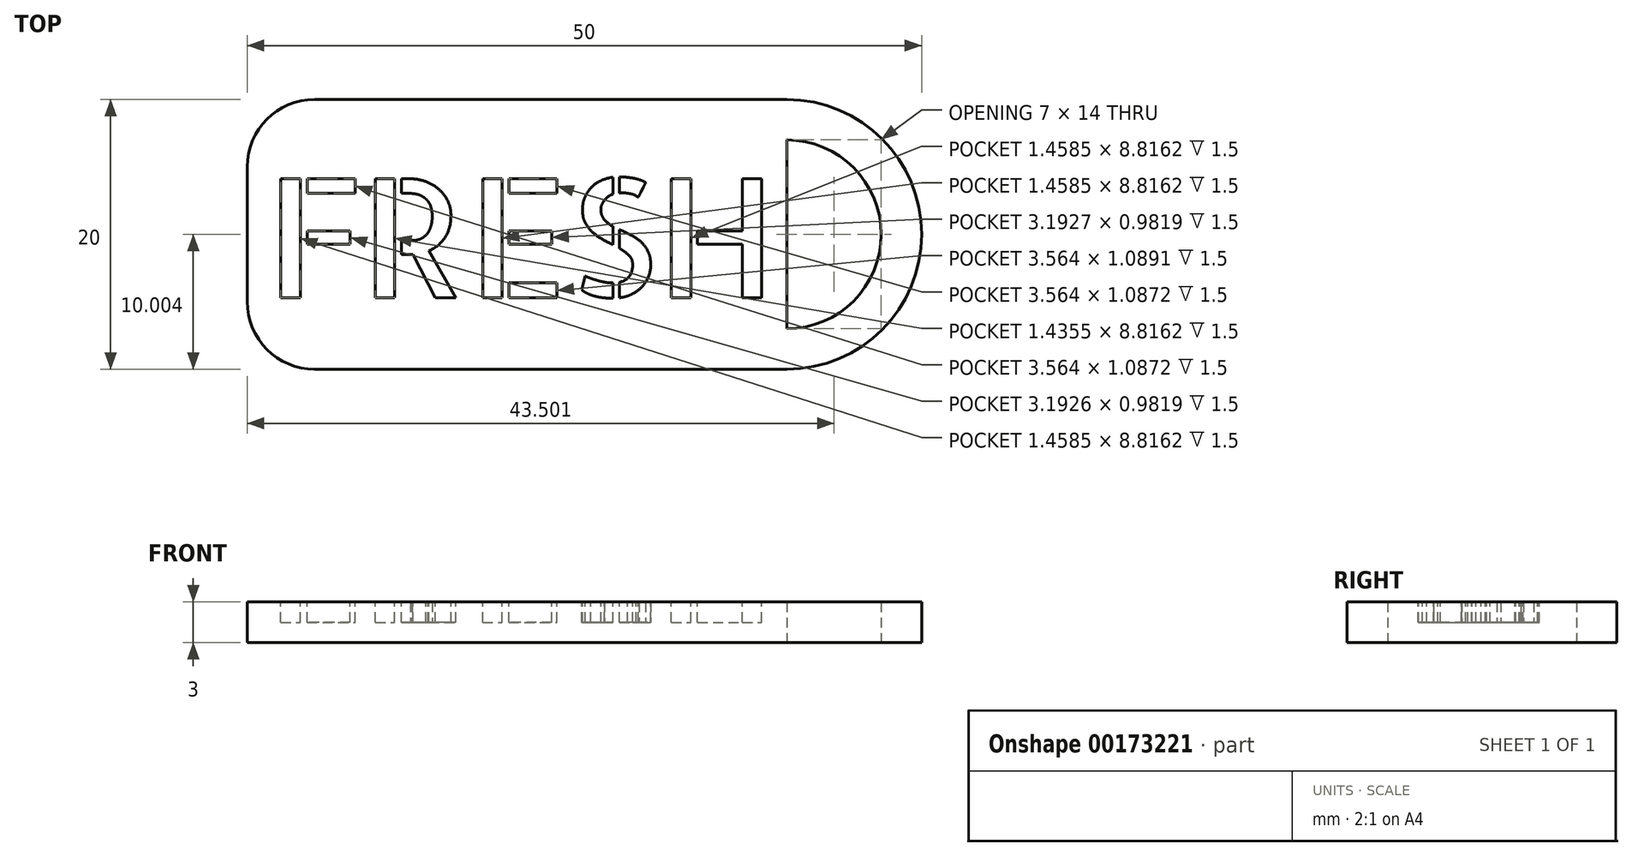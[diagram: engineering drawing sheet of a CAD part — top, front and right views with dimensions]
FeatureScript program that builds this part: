
annotation { "Feature Type Name" : "Feature", "Feature Type Description" : "" }
export const myFeature = defineFeature(function(context is Context, id is Id, definition is map)
    precondition{}
    {
        {
            var Q0;
            Q0=qCreatedBy(makeId("Top.planeOp"),FACE);
            var sketch = newSketch(context, id + "F0", { "sketchPlane" : qUnion([Q0])});
            skLineSegment(sketch, "E0.bottom", {"start": v(-15.52, 12.91) * mm, "end": v(19.48, 12.91) * mm});
            skLineSegment(sketch, "E0.top", {"start": v(-15.52, -7.09) * mm, "end": v(19.48, -7.09) * mm});
            skLineSegment(sketch, "E0.left", {"start": v(-20.52, 7.91) * mm, "end": v(-20.52, -2.09) * mm});
            skLineSegment(sketch, "E0.right", {"start": v(19.48, 12.91) * mm, "end": v(19.48, -7.09) * mm});
            skArc(sketch, "E1", {"start": v(19.48, -7.09) * mm, "mid": v(29.48, 2.91) * mm, "end": v(19.48, 12.91) * mm});
            skArc(sketch, "E2", {"start": v(19.48, -4.09) * mm, "mid": v(26.48, 2.91) * mm, "end": v(19.48, 9.91) * mm});
            skPoint(sketch, "E3.visualSharp", {"position": v(-20.52, 12.91) * mm});
            skArc(sketch, "E3.filletArc", {"start": v(-15.52, 12.91) * mm, "mid": v(-19.06, 11.45) * mm, "end": v(-20.52, 7.91) * mm});
            skPoint(sketch, "E4.visualSharp", {"position": v(-20.52, -7.09) * mm});
            skArc(sketch, "E4.filletArc", {"start": v(-20.52, -2.09) * mm, "mid": v(-19.06, -5.62) * mm, "end": v(-15.52, -7.09) * mm});
            skSolve(sketch);
        }
        {
            var Q0;
            {var subQ2=sQuery(id+"F0.wireOp",EDGE,"E0.bottom");Q0=makeQuery(id+"F0.imprint","IMPRINT",FACE,{"disambiguationData":[TD([[makeQuery(id+"F0.imprint","IMPRINT",EDGE,{"derivedFrom":subQ2}),-1.0]])]});}
            var Q1;
            {var subQ0=sQuery(id+"F0.wireOp",EDGE,"E1");Q1=makeQuery(id+"F0.imprint","IMPRINT",FACE,{"disambiguationData":[TD([[makeQuery(id+"F0.imprint","IMPRINT",EDGE,{"derivedFrom":subQ0}),1.0]])]});}
            extrude(context, id + "F1", {"entities" : qUnion([Q0, Q1]), "depth" : 3 * mm});
        }
        {
            var Q0;
            Q0=makeQuery(id+"F1.opExtrude","CAP_FACE",FACE,{"disambiguationData":[OSD([sQuery(id+"F0.wireOp",EDGE,"E0.bottom"),sQuery(id+"F0.wireOp",EDGE,"E0.top"),sQuery(id+"F0.wireOp",EDGE,"E0.left"),sQuery(id+"F0.wireOp",EDGE,"E0.right"),sQuery(id+"F0.wireOp",EDGE,"E1"),sQuery(id+"F0.wireOp",EDGE,"E2"),sQuery(id+"F0.wireOp",EDGE,"E3.filletArc"),sQuery(id+"F0.wireOp",EDGE,"E4.filletArc")])],"isStart":false});
            var sketch = newSketch(context, id + "F2", { "sketchPlane" : qUnion([Q0])});
            skText(sketch, "E5", { "text": "FRESH", "fontName": "AllertaStencil-Regular.ttf"});
            const initialGuessF2  = {"E5": [-0.01917, -0.00178, 1, 0, 0.00882]};
            skSetInitialGuess(sketch, initialGuessF2);
            skSolve(sketch);
        }
        {
            var Q0;
            Q0 = qSketchRegion(id + "F2", true);
            extrude(context, id + "F3", {"entities" : qUnion([Q0]), "operationType" : NewBodyOperationType.REMOVE, "oppositeDirection" : true, "depth" : 1.5 * mm});
        }
    });
